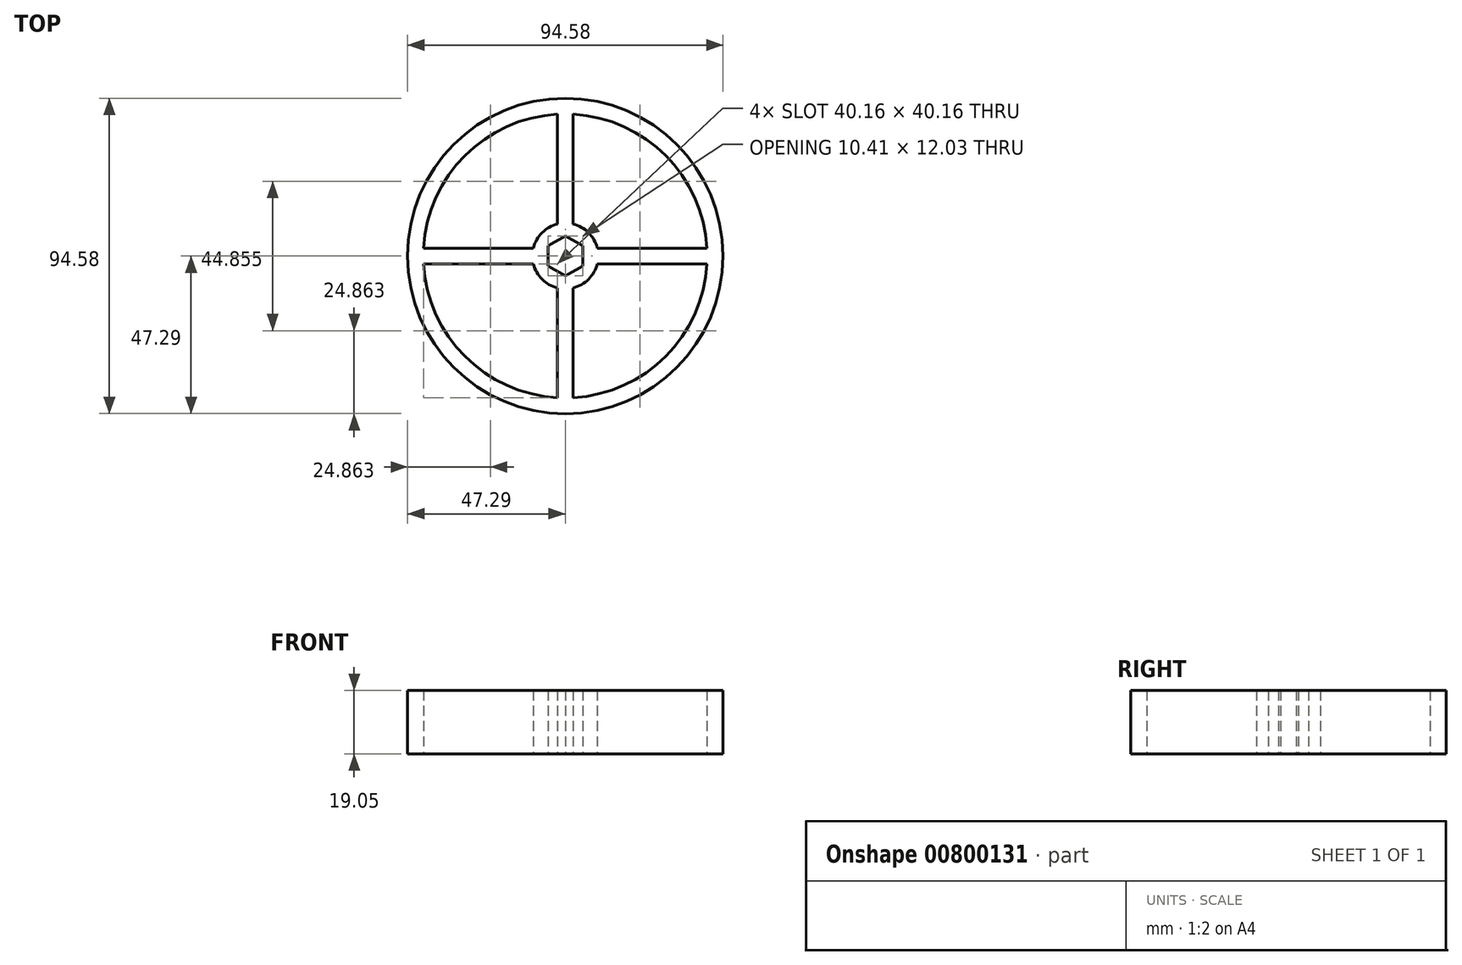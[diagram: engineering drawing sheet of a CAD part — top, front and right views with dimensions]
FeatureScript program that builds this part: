
annotation { "Feature Type Name" : "Feature", "Feature Type Description" : "" }
export const myFeature = defineFeature(function(context is Context, id is Id, definition is map)
    precondition{}
    {
        {
            var Q0;
            Q0=qCreatedBy(makeId("Top.planeOp"),FACE);
            var sketch = newSketch(context, id + "F0", { "sketchPlane" : qUnion([Q0])});
            skCircle(sketch, "E0.cCircle", {"center": v(0, 0) * mm, "radius": 5.2 * mm, "construction": true});
            skLineSegment(sketch, "E0.0", {"start": v(0, 6.01) * mm, "end": v(5.2, 3) * mm});
            skLineSegment(sketch, "E0.1", {"start": v(5.2, 3) * mm, "end": v(5.2, -3) * mm});
            skLineSegment(sketch, "E0.2", {"start": v(5.2, -3) * mm, "end": v(0, -6.01) * mm});
            skLineSegment(sketch, "E0.3", {"start": v(0, -6.01) * mm, "end": v(-5.2, -3) * mm});
            skLineSegment(sketch, "E0.4", {"start": v(-5.2, -3) * mm, "end": v(-5.2, 3) * mm});
            skLineSegment(sketch, "E0.5", {"start": v(-5.2, 3) * mm, "end": v(0, 6.01) * mm});
            skPoint(sketch, "E0.0.midPoint", {"position": v(2.6, 4.5) * mm});
            skCircle(sketch, "E1", {"center": v(0, 0) * mm, "radius": 47.3 * mm});
            skCircle(sketch, "E2", {"center": v(0, 0) * mm, "radius": 42.57 * mm});
            skCircle(sketch, "E3", {"center": v(0, 0) * mm, "radius": 9.87 * mm});
            skLineSegment(sketch, "E4", {"start": v(-2.35, 42.5) * mm, "end": v(-2.35, 9.58) * mm});
            skLineSegment(sketch, "E5", {"start": v(2.35, 42.5) * mm, "end": v(2.35, 9.58) * mm});
            skLineSegment(sketch, "E6.1.0", {"start": v(-42.5, -2.35) * mm, "end": v(-9.58, -2.35) * mm});
            skLineSegment(sketch, "E6.1.1", {"start": v(-42.5, 2.35) * mm, "end": v(-9.58, 2.35) * mm});
            skLineSegment(sketch, "E6.2.0", {"start": v(2.35, -42.5) * mm, "end": v(2.35, -9.58) * mm});
            skLineSegment(sketch, "E6.2.1", {"start": v(-2.35, -42.5) * mm, "end": v(-2.35, -9.58) * mm});
            skLineSegment(sketch, "E6.3.0", {"start": v(42.5, 2.35) * mm, "end": v(9.58, 2.35) * mm});
            skLineSegment(sketch, "E6.3.1", {"start": v(42.5, -2.35) * mm, "end": v(9.58, -2.35) * mm});
            skSolve(sketch);
        }
        {
            var Q0;
            Q0=makeQuery(id+"F0.imprint","IMPRINT",FACE,{"disambiguationData":[TD([[makeQuery(id+"F0.imprint","IMPRINT",EDGE,{"derivedFrom":sQuery(id+"F0.wireOp",EDGE,"E1")}),1.0]])]});
            var Q1;
            {var subQ0=sQuery(id+"F0.wireOp",EDGE,"E4");Q1=makeQuery(id+"F0.imprint","IMPRINT",FACE,{"disambiguationData":[TD([[makeQuery(id+"F0.imprint","IMPRINT",EDGE,{"derivedFrom":subQ0}),1.0]])]});}
            var Q2;
            Q2=makeQuery(id+"F0.imprint","IMPRINT",FACE,{"disambiguationData":[TD([[makeQuery(id+"F0.imprint","IMPRINT",EDGE,{"derivedFrom":sQuery(id+"F0.wireOp",EDGE,"E0.0")}),1.0]])]});
            var Q3;
            {var subQ0=sQuery(id+"F0.wireOp",EDGE,"E6.1.0");Q3=makeQuery(id+"F0.imprint","IMPRINT",FACE,{"disambiguationData":[TD([[makeQuery(id+"F0.imprint","IMPRINT",EDGE,{"derivedFrom":subQ0}),1.0]])]});}
            var Q4;
            {var subQ0=sQuery(id+"F0.wireOp",EDGE,"E6.2.0");Q4=makeQuery(id+"F0.imprint","IMPRINT",FACE,{"disambiguationData":[TD([[makeQuery(id+"F0.imprint","IMPRINT",EDGE,{"derivedFrom":subQ0}),1.0]])]});}
            var Q5;
            {var subQ0=sQuery(id+"F0.wireOp",EDGE,"E6.3.0");Q5=makeQuery(id+"F0.imprint","IMPRINT",FACE,{"disambiguationData":[TD([[makeQuery(id+"F0.imprint","IMPRINT",EDGE,{"derivedFrom":subQ0}),1.0]])]});}
            extrude(context, id + "F1", {"entities" : qUnion([Q0, Q1, Q2, Q3, Q4, Q5]), "depth" : 19.05 * mm, "offsetDistance" : 25.4 * mm});
        }
    });
